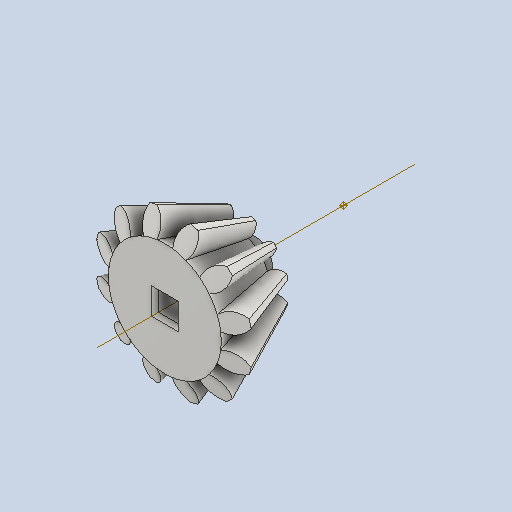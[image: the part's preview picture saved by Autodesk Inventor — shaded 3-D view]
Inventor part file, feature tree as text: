
AUTODESK INVENTOR PART (.ipt)
format: ipt  version: 2022 (Build 260153000, 153)  size: 498,176 bytes
history: native  units: in
note: dims shown in document units (in); Inventor stores cm internally (conversion verified against a paired STEP export)
features: other x30, sketch x3
ambient origin geometry x8: Origin, YZ Plane, XZ Plane, XY Plane, X Axis, Y Axis, Z Axis, Center Point
bodies: Solid1 (feature_tree)
feature tree (33):
  other  "Bevel Gear11_MIR1_MIR.ipt"
  other  "Solid1::Bevel Gear11_MIR1_MIR.ipt"
  other  "TaggingFeature1"
  other  "Teeth Body Sketch"
  other  "Start Sketch"
  other  "End Sketch"
  other  "End Sketch Right"
  other  "End Sketch Left"
  other  "Body Sketch"
  sketch  "Sketch6"  dims[d0=0.3937in]
  sketch  "Sketch8"  dims[d48=0.0in d49=0.0in d50=90.0deg d52=0.0in d53=0.0in d54=0.0in]
  sketch  "Sketch9"
  other  "3D Sketch Right"
  other  "3D Sketch Left"
  other  "Mesh Plane"
  other  "Top Plane"
  other  "Mesh Plane2"
  other  "Tooth Plane"
  other  "End Plane"
  other  "End Plane Right"
  other  "End Plane Left"
  other  "Z Axis_1"
  other  "Top Point"
  other  "Start Point"
  other  "End Point"
  other  "Srf1"
  other  "Srf1::Derived"
  other  "Start plane iMate"
  other  "Mesh iMate2"
  other  "Axis Angle iMate"
  other  "Axis iMate"
  other  "Mesh iMate"
  other  "Intersection iMate"
